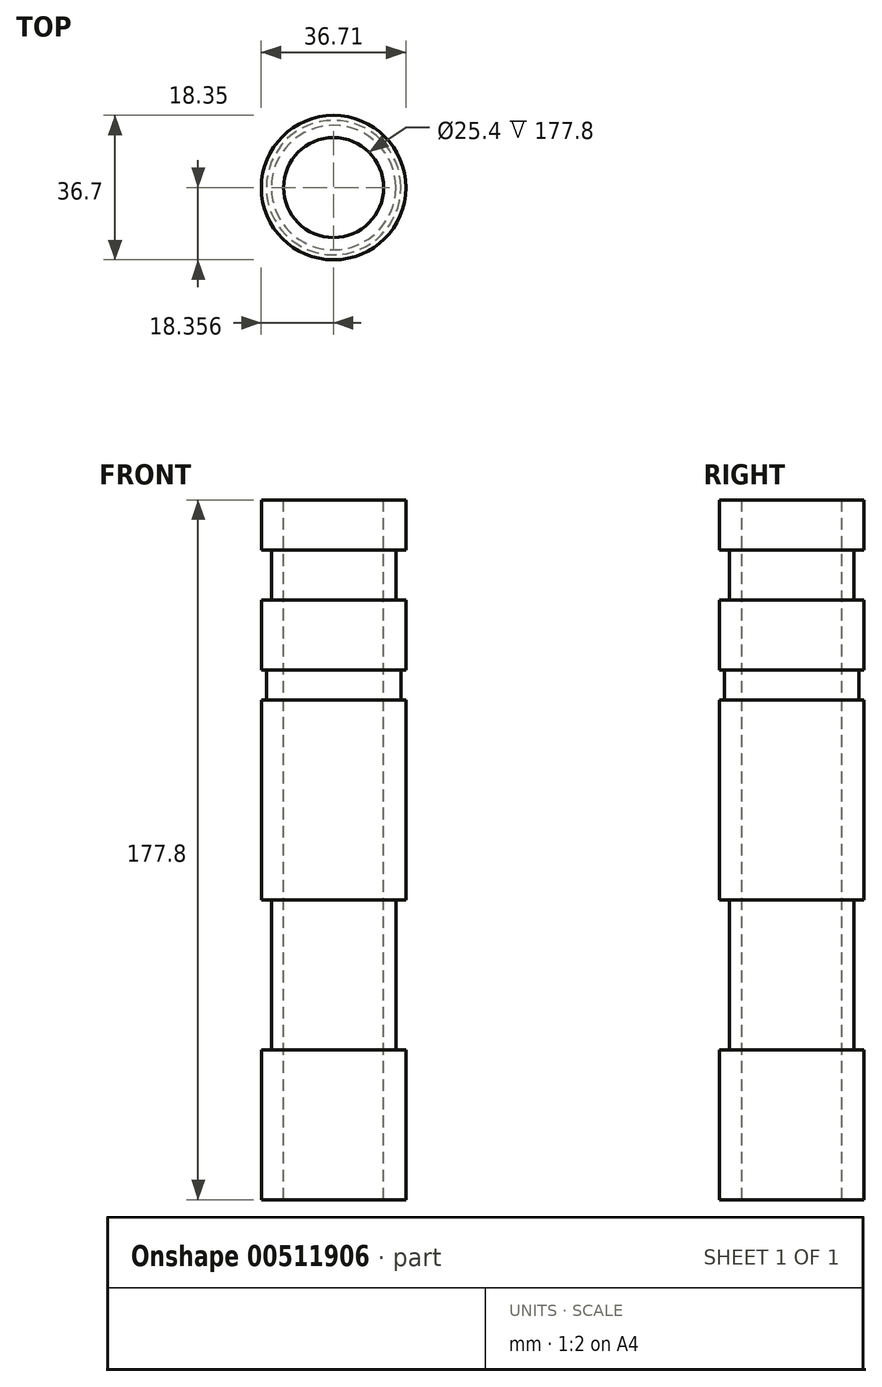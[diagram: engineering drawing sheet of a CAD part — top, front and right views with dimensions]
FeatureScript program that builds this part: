
annotation { "Feature Type Name" : "Feature", "Feature Type Description" : "" }
export const myFeature = defineFeature(function(context is Context, id is Id, definition is map)
    precondition{}
    {
        {
            var Q0;
            Q0=qCreatedBy(makeId("Front.planeOp"),FACE);
            var sketch = newSketch(context, id + "F0", { "sketchPlane" : qUnion([Q0])});
            skLineSegment(sketch, "E0.left", {"start": v(17.37, 72.05) * mm, "end": v(17.37, 59.35) * mm});
            skPoint(sketch, "E0.middle", {"position": v(0, 0) * mm});
            skLineSegment(sketch, "E1", {"start": v(17.37, 59.35) * mm, "end": v(14.83, 59.35) * mm});
            skLineSegment(sketch, "E2", {"start": v(14.83, 59.35) * mm, "end": v(14.83, 46.65) * mm});
            skLineSegment(sketch, "E3", {"start": v(14.83, 46.65) * mm, "end": v(17.37, 46.65) * mm});
            skLineSegment(sketch, "E4.trimOffspring", {"start": v(17.37, 46.65) * mm, "end": v(17.37, 28.87) * mm});
            skLineSegment(sketch, "E5", {"start": v(-0.98, 101.6) * mm, "end": v(-0.98, -101.6) * mm});
            skLineSegment(sketch, "E6", {"start": v(11.72, 72.05) * mm, "end": v(11.72, -105.75) * mm});
            skLineSegment(sketch, "E7", {"start": v(11.72, -105.75) * mm, "end": v(17.37, -105.75) * mm});
            skLineSegment(sketch, "E8", {"start": v(11.72, 72.05) * mm, "end": v(17.37, 72.05) * mm});
            skLineSegment(sketch, "E9", {"start": v(17.37, 28.87) * mm, "end": v(16.1, 28.87) * mm});
            skLineSegment(sketch, "E10", {"start": v(16.1, 28.87) * mm, "end": v(16.1, 21.25) * mm});
            skLineSegment(sketch, "E11", {"start": v(16.1, 21.25) * mm, "end": v(17.37, 21.25) * mm});
            skLineSegment(sketch, "E12.trimOffspring", {"start": v(17.37, 21.25) * mm, "end": v(17.37, -29.55) * mm});
            skLineSegment(sketch, "E13", {"start": v(17.37, -29.55) * mm, "end": v(14.83, -29.55) * mm});
            skLineSegment(sketch, "E14", {"start": v(14.83, -29.55) * mm, "end": v(14.83, -67.65) * mm});
            skLineSegment(sketch, "E15", {"start": v(14.83, -67.65) * mm, "end": v(17.37, -67.65) * mm});
            skLineSegment(sketch, "E16.trimOffspring", {"start": v(17.37, -67.65) * mm, "end": v(17.37, -105.75) * mm});
            skSolve(sketch);
        }
        {
            var Q0;
            Q0=makeQuery(id+"F0.imprint","IMPRINT",FACE,{"disambiguationData":[TD([[makeQuery(id+"F0.imprint","IMPRINT",EDGE,{"derivedFrom":sQuery(id+"F0.wireOp",EDGE,"E0.left")}),-1.0]])]});
            var Q1;
            Q1=sQuery(id+"F0.wireOp",EDGE,"E5");
            revolve(context, id + "F1", {"entities" : qUnion([Q0]), "axis" : qUnion([Q1]), "revolveType" : RevolveType.FULL});
        }
    });
